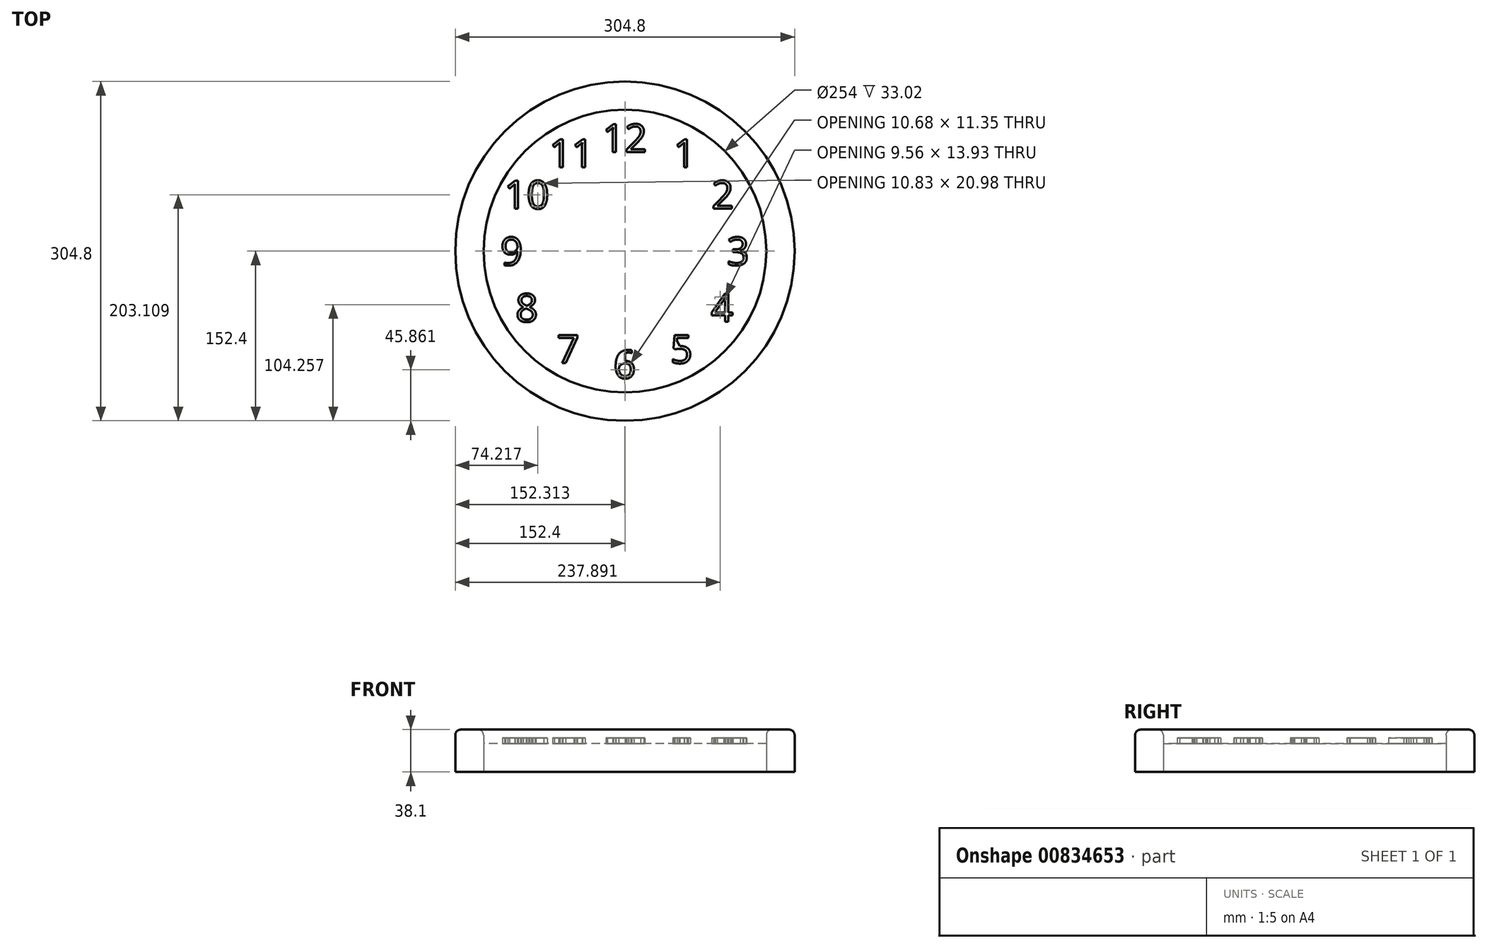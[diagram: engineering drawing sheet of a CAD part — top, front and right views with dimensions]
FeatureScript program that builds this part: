
annotation { "Feature Type Name" : "Feature", "Feature Type Description" : "" }
export const myFeature = defineFeature(function(context is Context, id is Id, definition is map)
    precondition{}
    {
        {
            var Q0;
            Q0=qCreatedBy(makeId("Top.planeOp"),FACE);
            var sketch = newSketch(context, id + "F0", { "sketchPlane" : qUnion([Q0])});
            skCircle(sketch, "E0", {"center": v(0, 0) * mm, "radius": 127 * mm});
            skCircle(sketch, "E1", {"center": v(0, 0) * mm, "radius": 152.4 * mm});
            skSolve(sketch);
        }
        {
            var Q0;
            Q0=makeQuery(id+"F0.imprint","IMPRINT",FACE,{"disambiguationData":[TD([[makeQuery(id+"F0.imprint","IMPRINT",EDGE,{"derivedFrom":sQuery(id+"F0.wireOp",EDGE,"E0")}),1.0]])]});
            extrude(context, id + "F1", {"entities" : qUnion([Q0]), "depth" : 25.4 * mm, "offsetDistance" : 25.4 * mm});
        }
        {
            var Q0;
            Q0=makeQuery(id+"F0.imprint","IMPRINT",FACE,{"disambiguationData":[TD([[makeQuery(id+"F0.imprint","IMPRINT",EDGE,{"derivedFrom":sQuery(id+"F0.wireOp",EDGE,"E0")}),-1.0]])]});
            extrude(context, id + "F2", {"entities" : qUnion([Q0]), "depth" : 38.1 * mm, "offsetDistance" : 25.4 * mm});
        }
        {
            var Q0;
            Q0=makeQuery(id+"F2.opExtrude","CAP_EDGE",EDGE,{"disambiguationData":[OSD([sQuery(id+"F0.wireOp",EDGE,"E0")])],"isStart":false});
            var Q1;
            Q1=makeQuery(id+"F2.opExtrude","CAP_EDGE",EDGE,{"disambiguationData":[OSD([sQuery(id+"F0.wireOp",EDGE,"E1")])],"isStart":false});
            fillet(context, id + "F3", {"entities" : qUnion([Q0, Q1]), "radius" : 5.08 * mm, "tangentPropagation" : true, "allowEdgeOverflow" : false});
        }
        {
            var Q0;
            Q0=makeQuery(id+"F1.opExtrude","CAP_FACE",FACE,{"disambiguationData":[OSD([sQuery(id+"F0.wireOp",EDGE,"E0")])],"isStart":false});
            cPlane(context, id + "F4", {"entities" : qUnion([Q0]), "cplaneType" : CPlaneType.OFFSET, "offset" : 0.25 * mm, "width" : 152.4 * mm, "height" : 152.4 * mm});
        }
        {
            var Q0;
            Q0=qCreatedBy(id+"F4.planeOp",FACE);
            var sketch = newSketch(context, id + "F5", { "sketchPlane" : qUnion([Q0])});
            skPoint(sketch, "E2", {"position": v(0, 0) * mm});
            skLineSegment(sketch, "E3", {"start": v(0, 0) * mm, "end": v(0, 101.6) * mm});
            skLineSegment(sketch, "E4", {"start": v(0, 0) * mm, "end": v(0, -101.6) * mm});
            skLineSegment(sketch, "E5.1.0", {"start": v(0, 0) * mm, "end": v(-50.8, 87.99) * mm});
            skLineSegment(sketch, "E5.1.1", {"start": v(0, 0) * mm, "end": v(50.8, -87.99) * mm});
            skLineSegment(sketch, "E5.2.0", {"start": v(0, 0) * mm, "end": v(-87.99, 50.8) * mm});
            skLineSegment(sketch, "E5.2.1", {"start": v(0, 0) * mm, "end": v(87.99, -50.8) * mm});
            skLineSegment(sketch, "E5.3.0", {"start": v(0, 0) * mm, "end": v(-101.6, 0) * mm});
            skLineSegment(sketch, "E5.3.1", {"start": v(0, 0) * mm, "end": v(101.6, 0) * mm});
            skLineSegment(sketch, "E5.4.0", {"start": v(0, 0) * mm, "end": v(-87.99, -50.8) * mm});
            skLineSegment(sketch, "E5.4.1", {"start": v(0, 0) * mm, "end": v(87.99, 50.8) * mm});
            skLineSegment(sketch, "E5.5.0", {"start": v(0, 0) * mm, "end": v(-50.8, -87.99) * mm});
            skLineSegment(sketch, "E5.5.1", {"start": v(0, 0) * mm, "end": v(50.8, 87.99) * mm});
            skLineSegment(sketch, "E5.7.0", {"start": v(0, 0) * mm, "end": v(50.8, -87.99) * mm});
            skLineSegment(sketch, "E5.7.1", {"start": v(0, 0) * mm, "end": v(-50.8, 87.99) * mm});
            skLineSegment(sketch, "E5.8.0", {"start": v(0, 0) * mm, "end": v(87.99, -50.8) * mm});
            skLineSegment(sketch, "E5.8.1", {"start": v(0, 0) * mm, "end": v(-87.99, 50.8) * mm});
            skLineSegment(sketch, "E5.9.0", {"start": v(0, 0) * mm, "end": v(101.6, 0) * mm});
            skLineSegment(sketch, "E5.9.1", {"start": v(0, 0) * mm, "end": v(-101.6, 0) * mm});
            skLineSegment(sketch, "E5.10.0", {"start": v(0, 0) * mm, "end": v(87.99, 50.8) * mm});
            skLineSegment(sketch, "E5.10.1", {"start": v(0, 0) * mm, "end": v(-87.99, -50.8) * mm});
            skLineSegment(sketch, "E5.11.0", {"start": v(0, 0) * mm, "end": v(50.8, 87.99) * mm});
            skLineSegment(sketch, "E5.11.1", {"start": v(0, 0) * mm, "end": v(-50.8, -87.99) * mm});
            skText(sketch, "E6", { "text": "12", "fontName": "OpenSans-Regular.ttf"});
            skPoint(sketch, "E7", {"position": v(0, 101.6) * mm});
            skText(sketch, "E8", { "text": "1\n", "fontName": "OpenSans-Regular.ttf"});
            skPoint(sketch, "E9", {"position": v(50.8, 87.99) * mm});
            skText(sketch, "E10", { "text": "2", "fontName": "OpenSans-Regular.ttf"});
            skPoint(sketch, "E11", {"position": v(87.99, 50.8) * mm});
            skText(sketch, "E12", { "text": "3\n", "fontName": "OpenSans-Regular.ttf"});
            skPoint(sketch, "E13", {"position": v(101.6, 0) * mm});
            skText(sketch, "E14", { "text": "4", "fontName": "OpenSans-Regular.ttf"});
            skPoint(sketch, "E15", {"position": v(87.99, -50.8) * mm});
            skText(sketch, "E16", { "text": "5", "fontName": "OpenSans-Regular.ttf"});
            skPoint(sketch, "E17", {"position": v(50.8, -87.99) * mm});
            skText(sketch, "E18", { "text": "6", "fontName": "OpenSans-Regular.ttf"});
            skPoint(sketch, "E19", {"position": v(0, -101.6) * mm});
            skText(sketch, "E20", { "text": "7", "fontName": "OpenSans-Regular.ttf"});
            skPoint(sketch, "E21", {"position": v(-50.8, -87.99) * mm});
            skText(sketch, "E22", { "text": "8", "fontName": "OpenSans-Regular.ttf"});
            skPoint(sketch, "E23", {"position": v(-87.99, -50.8) * mm});
            skText(sketch, "E24", { "text": "9", "fontName": "OpenSans-Regular.ttf"});
            skPoint(sketch, "E25", {"position": v(-101.6, 0) * mm});
            skText(sketch, "E26", { "text": "10", "fontName": "OpenSans-Regular.ttf"});
            skPoint(sketch, "E27", {"position": v(-87.99, 50.8) * mm});
            skText(sketch, "E28", { "text": "11", "fontName": "OpenSans-Regular.ttf"});
            skPoint(sketch, "E29", {"position": v(-50.8, 87.99) * mm});
            const initialGuessF5  = {"E6": [-0.02037, 0.0889, 1, 0, 0.0254], "E8": [0.0435, 0.07529, 1, 0, 0.0254], "E10": [0.0777, 0.0381, 1, 0, 0.0254], "E12": [0.0914, -0.0127, 1, 0, 0.0254], "E14": [0.07711, -0.0635, 1, 0, 0.0254], "E16": [0.04059, -0.10069, 1, 0, 0.0254], "E18": [-0.01037, -0.1143, 1, 0, 0.0254], "E20": [-0.06113, -0.10069, 1, 0, 0.0254], "E22": [-0.0983, -0.0635, 1, 0, 0.0254], "E24": [-0.11188, -0.0127, 1, 0, 0.0254], "E26": [-0.10842, 0.0381, 1, 0, 0.0254], "E28": [-0.06819, 0.07529, 1, 0, 0.0254]};
            skSetInitialGuess(sketch, initialGuessF5);
            skSolve(sketch);
        }
        {
            var Q0;
            Q0 = qSketchRegion(id + "F5", true);
            extrude(context, id + "F6", {"entities" : qUnion([Q0]), "depth" : 5.08 * mm, "offsetDistance" : 25.4 * mm});
        }
    });
